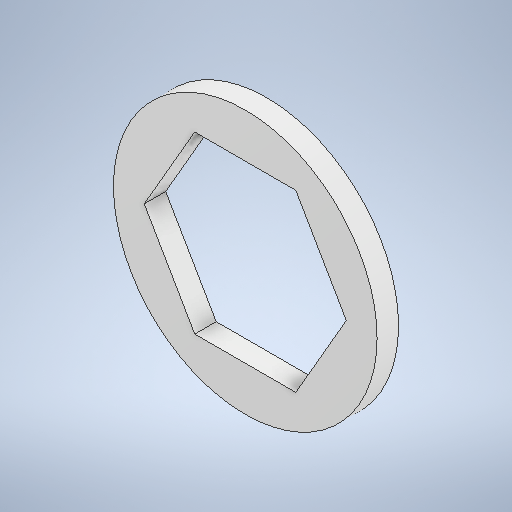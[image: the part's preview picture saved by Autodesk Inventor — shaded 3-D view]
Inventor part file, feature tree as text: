
AUTODESK INVENTOR PART (.ipt)
format: ipt  version: 2025.1 (Build 291241020, 241B)  size: 250,880 bytes
history: native  units: in
note: dims shown in document units (in); Inventor stores cm internally (conversion verified against a paired STEP export)
features: extrude x1, sketch x1
ambient origin geometry x8: Origin, YZ Plane, XZ Plane, XY Plane, X Axis, Y Axis, Z Axis, Center Point
bodies: Solid1 (feature_tree)
feature tree (2):
  extrude  "Extrusion1"  Depth=0.51in
  sketch  "Sketch1"  dims[d0=0.768in d1=0.51in d2=0.0625in d3=0.0in]
